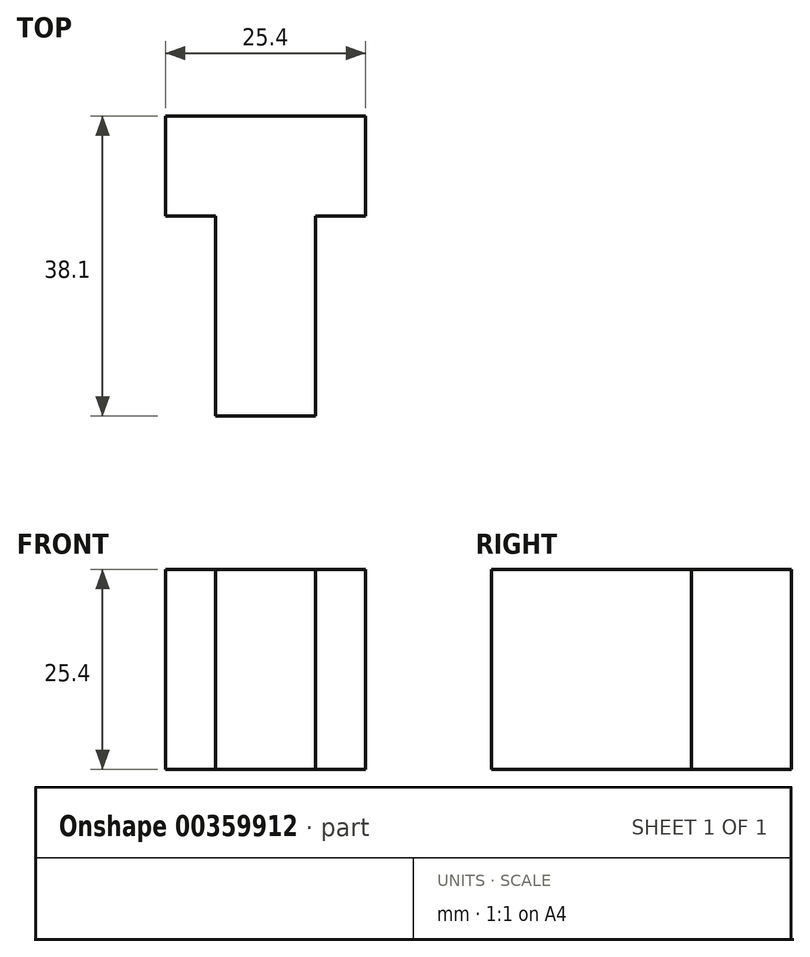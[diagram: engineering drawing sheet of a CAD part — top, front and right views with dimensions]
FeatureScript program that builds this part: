
annotation { "Feature Type Name" : "Feature", "Feature Type Description" : "" }
export const myFeature = defineFeature(function(context is Context, id is Id, definition is map)
    precondition{}
    {
        {
            var Q0;
            Q0=qCreatedBy(makeId("Top.planeOp"),FACE);
            var sketch = newSketch(context, id + "F0", { "sketchPlane" : qUnion([Q0])});
            skLineSegment(sketch, "E0", {"start": v(0, 38.1) * mm, "end": v(0, 25.4) * mm});
            skLineSegment(sketch, "E1", {"start": v(0, 38.1) * mm, "end": v(25.4, 38.1) * mm});
            skLineSegment(sketch, "E2", {"start": v(25.4, 38.1) * mm, "end": v(25.4, 25.4) * mm});
            skLineSegment(sketch, "E3", {"start": v(0, 25.4) * mm, "end": v(6.35, 25.4) * mm});
            skLineSegment(sketch, "E4", {"start": v(6.35, 25.4) * mm, "end": v(6.35, 0) * mm});
            skLineSegment(sketch, "E5", {"start": v(25.4, 25.4) * mm, "end": v(19.05, 25.4) * mm});
            skLineSegment(sketch, "E6", {"start": v(19.05, 25.4) * mm, "end": v(19.05, 0) * mm});
            skLineSegment(sketch, "E7", {"start": v(6.35, 0) * mm, "end": v(19.05, 0) * mm});
            skSolve(sketch);
        }
        {
            var Q0;
            Q0 = qSketchRegion(id + "F0", true);
            extrude(context, id + "F1", {"entities" : qUnion([Q0]), "depth" : 25.4 * mm});
        }
        {
            var Q0;
            Q0 = qSketchRegion(id + "F0", true);
            extrude(context, id + "F2", {"entities" : qUnion([Q0]), "operationType" : NewBodyOperationType.ADD, "depth" : 25.4 * mm});
        }
    });
